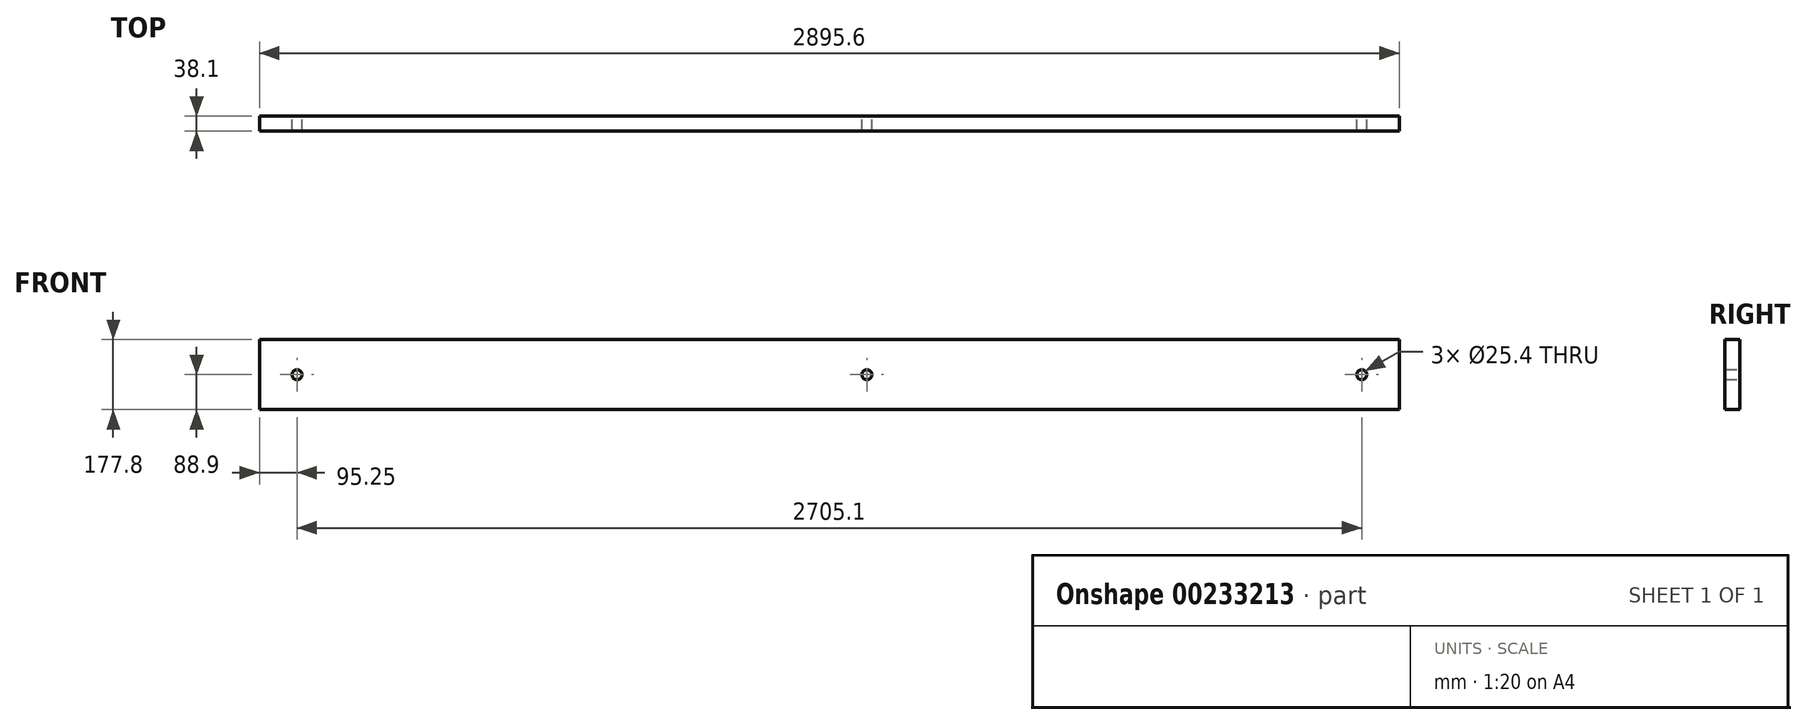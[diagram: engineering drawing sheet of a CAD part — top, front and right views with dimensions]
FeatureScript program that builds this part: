
annotation { "Feature Type Name" : "Feature", "Feature Type Description" : "" }
export const myFeature = defineFeature(function(context is Context, id is Id, definition is map)
    precondition{}
    {
        {
            var Q0;
            Q0=qCreatedBy(makeId("Front.planeOp"),FACE);
            var sketch = newSketch(context, id + "F0", { "sketchPlane" : qUnion([Q0])});
            skLineSegment(sketch, "E0.bottom", {"start": v(-1449.98, -1332.83) * mm, "end": v(1445.62, -1332.83) * mm});
            skLineSegment(sketch, "E0.top", {"start": v(-1449.98, -1510.63) * mm, "end": v(1445.62, -1510.63) * mm});
            skLineSegment(sketch, "E0.left", {"start": v(-1449.98, -1332.83) * mm, "end": v(-1449.98, -1510.63) * mm});
            skLineSegment(sketch, "E0.right", {"start": v(1445.62, -1332.83) * mm, "end": v(1445.62, -1510.63) * mm});
            skCircle(sketch, "E1", {"center": v(-1354.73, -1421.73) * mm, "radius": 12.7 * mm});
            skCircle(sketch, "E2", {"center": v(1350.37, -1421.73) * mm, "radius": 12.7 * mm});
            skCircle(sketch, "E3", {"center": v(93.07, -1421.73) * mm, "radius": 12.7 * mm});
            skSolve(sketch);
        }
        {
            var Q0;
            Q0=makeQuery(id+"F0.imprint","IMPRINT",FACE,{"disambiguationData":[TD([[makeQuery(id+"F0.imprint","IMPRINT",EDGE,{"derivedFrom":sQuery(id+"F0.wireOp",EDGE,"E0.bottom")}),-1.0]])]});
            extrude(context, id + "F1", {"entities" : qUnion([Q0]), "depth" : 38.1 * mm});
        }
    });
